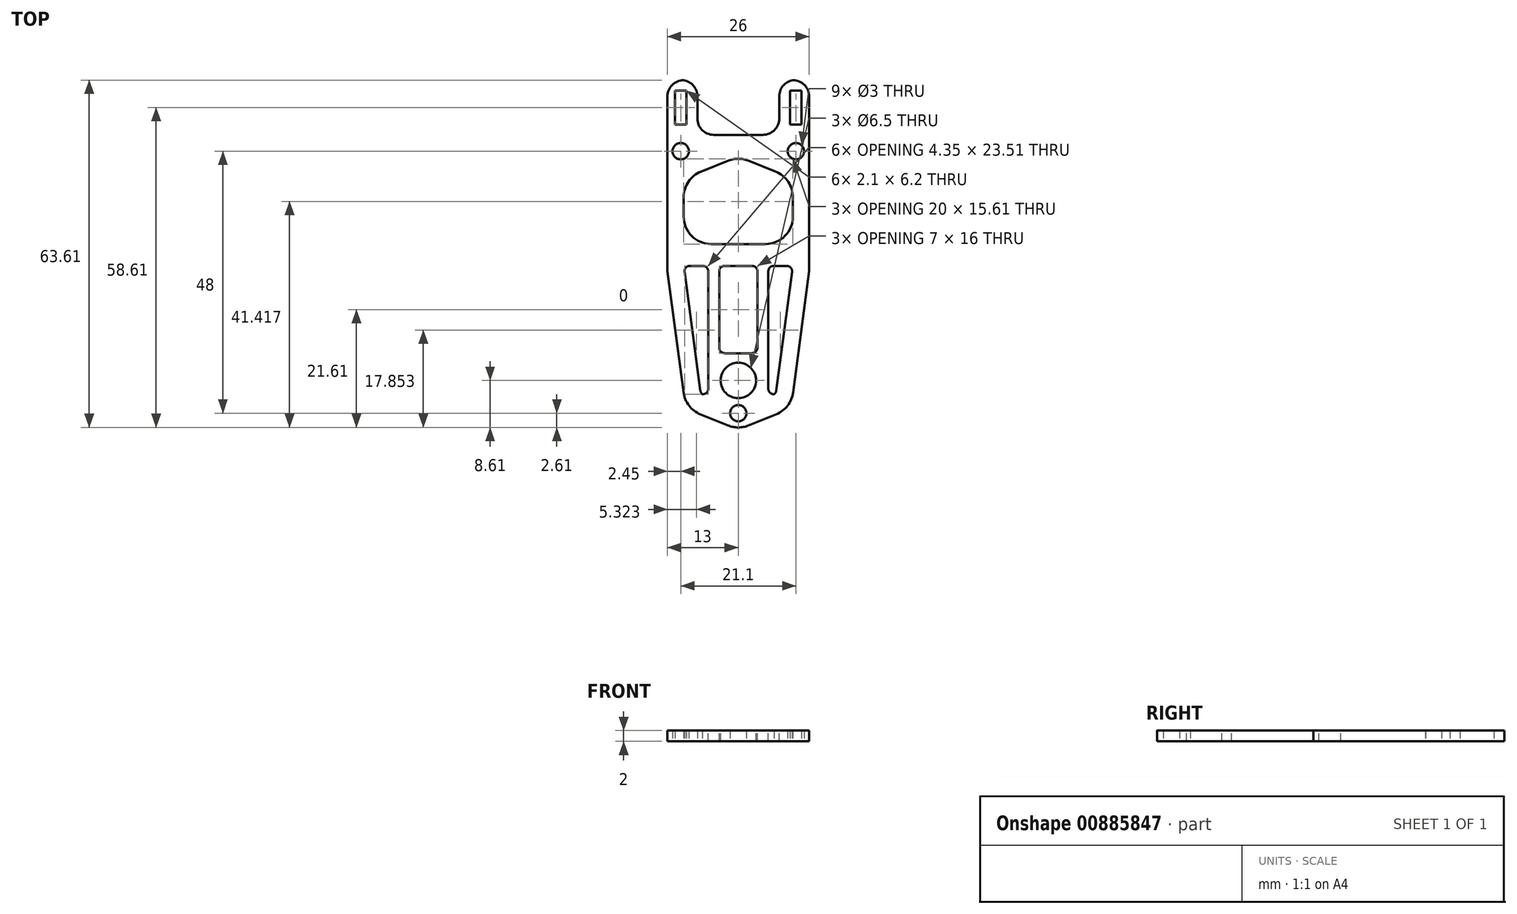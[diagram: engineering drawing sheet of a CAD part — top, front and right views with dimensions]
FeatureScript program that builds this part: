
annotation { "Feature Type Name" : "Feature", "Feature Type Description" : "" }
export const myFeature = defineFeature(function(context is Context, id is Id, definition is map)
    precondition{}
    {
        {
            var Q0;
            Q0=qCreatedBy(makeId("Top.planeOp"),FACE);
            var sketch = newSketch(context, id + "F0", { "sketchPlane" : qUnion([Q0])});
            skLineSegment(sketch, "E0.top", {"start": v(13, -32) * mm, "end": v(-13, -32) * mm});
            skLineSegment(sketch, "E0.left", {"start": v(13, 32) * mm, "end": v(13, -32) * mm});
            skLineSegment(sketch, "E0.right", {"start": v(-13, 32) * mm, "end": v(-13, -32) * mm});
            skPoint(sketch, "E0.middle", {"position": v(0, 0) * mm});
            skLineSegment(sketch, "E1.bottom", {"start": v(-11.6, 30.1) * mm, "end": v(-9.5, 30.1) * mm});
            skLineSegment(sketch, "E1.top", {"start": v(-11.6, 23.9) * mm, "end": v(-9.5, 23.9) * mm});
            skLineSegment(sketch, "E1.left", {"start": v(-11.6, 30.1) * mm, "end": v(-11.6, 23.9) * mm});
            skLineSegment(sketch, "E1.right", {"start": v(-9.5, 30.1) * mm, "end": v(-9.5, 23.9) * mm});
            skLineSegment(sketch, "E2.bottom", {"start": v(9.5, 30.1) * mm, "end": v(11.6, 30.1) * mm});
            skLineSegment(sketch, "E2.top", {"start": v(9.5, 23.9) * mm, "end": v(11.6, 23.9) * mm});
            skLineSegment(sketch, "E2.left", {"start": v(9.5, 30.1) * mm, "end": v(9.5, 23.9) * mm});
            skLineSegment(sketch, "E2.right", {"start": v(11.6, 30.1) * mm, "end": v(11.6, 23.9) * mm});
            skCircle(sketch, "E3", {"center": v(-10.55, 19) * mm, "radius": 1.5 * mm});
            skPoint(sketch, "E3.centerSnap0", {"position": v(-10.55, 30.1) * mm});
            skCircle(sketch, "E4", {"center": v(10.55, 19) * mm, "radius": 1.5 * mm});
            skPoint(sketch, "E4.centerSnap0", {"position": v(10.55, 30.1) * mm});
            skCircle(sketch, "E5", {"center": v(0, -29) * mm, "radius": 1.5 * mm});
            skLineSegment(sketch, "E6", {"start": v(-7.5, 32) * mm, "end": v(-7.5, 22) * mm});
            skLineSegment(sketch, "E7", {"start": v(-7.5, 22) * mm, "end": v(7.5, 22) * mm});
            skLineSegment(sketch, "E8", {"start": v(7.5, 22) * mm, "end": v(7.5, 32) * mm});
            skLineSegment(sketch, "E9", {"start": v(-13, 32) * mm, "end": v(-7.5, 32) * mm});
            skLineSegment(sketch, "E10", {"start": v(7.5, 32) * mm, "end": v(13, 32) * mm});
            skSolve(sketch);
        }
        {
            var Q0;
            Q0 = qSketchRegion(id + "F0", true);
            extrude(context, id + "F1", {"entities" : qUnion([Q0]), "depth" : 2 * mm, "offsetDistance" : 25 * mm});
        }
        {
            var Q0;
            Q0=makeQuery(id+"F1.opExtrude","SWEPT_EDGE",EDGE,{"disambiguationData":[OSD([sQuery(id+"F0.wireOp",EDGE,"E0.bottom"),sQuery(id+"F0.wireOp",EDGE,"E0.right")])]});
            var Q1;
            Q1=makeQuery(id+"F1.opExtrude","SWEPT_EDGE",EDGE,{"disambiguationData":[OSD([sQuery(id+"F0.wireOp",EDGE,"E0.bottom"),sQuery(id+"F0.wireOp",EDGE,"E0.left")])]});
            fillet(context, id + "F2", {"entities" : qUnion([Q0, Q1]), "radius" : 3 * mm, "tangentPropagation" : true, "allowEdgeOverflow" : false});
        }
        {
            var Q0;
            Q0=makeQuery(id+"F1.opExtrude","CAP_FACE",FACE,{"disambiguationData":[OSD([sQuery(id+"F0.wireOp",EDGE,"E0.bottom"),sQuery(id+"F0.wireOp",EDGE,"E0.top"),sQuery(id+"F0.wireOp",EDGE,"E0.left"),sQuery(id+"F0.wireOp",EDGE,"E0.right"),sQuery(id+"F0.wireOp",EDGE,"E1.bottom"),sQuery(id+"F0.wireOp",EDGE,"E1.top"),sQuery(id+"F0.wireOp",EDGE,"E1.left"),sQuery(id+"F0.wireOp",EDGE,"E1.right"),sQuery(id+"F0.wireOp",EDGE,"E2.bottom"),sQuery(id+"F0.wireOp",EDGE,"E2.top"),sQuery(id+"F0.wireOp",EDGE,"E2.left"),sQuery(id+"F0.wireOp",EDGE,"E2.right"),sQuery(id+"F0.wireOp",EDGE,"E3"),sQuery(id+"F0.wireOp",EDGE,"E4"),sQuery(id+"F0.wireOp",EDGE,"E5")])],"isStart":false});
            var sketch = newSketch(context, id + "F3", { "sketchPlane" : qUnion([Q0])});
            skLineSegment(sketch, "E11", {"start": v(-13, -3) * mm, "end": v(-13, -33) * mm});
            skLineSegment(sketch, "E12", {"start": v(-13, -33) * mm, "end": v(13, -33) * mm});
            skLineSegment(sketch, "E13", {"start": v(13, -33) * mm, "end": v(13, -3) * mm});
            skLineSegment(sketch, "E14", {"start": v(-13, -3) * mm, "end": v(-9.65, -28.1) * mm});
            skLineSegment(sketch, "E15", {"start": v(-9.65, -28.1) * mm, "end": v(0, -32) * mm});
            skLineSegment(sketch, "E16", {"start": v(0, -32) * mm, "end": v(9.65, -28.1) * mm});
            skLineSegment(sketch, "E17", {"start": v(9.65, -28.1) * mm, "end": v(13, -3) * mm});
            skSolve(sketch);
        }
        {
            var Q0;
            Q0 = qSketchRegion(id + "F3", true);
            extrude(context, id + "F4", {"entities" : qUnion([Q0]), "operationType" : NewBodyOperationType.REMOVE, "endBound" : BoundingType.THROUGH_ALL, "oppositeDirection" : true, "depth" : 25 * mm, "offsetDistance" : 25 * mm});
        }
        {
            var Q0;
            Q0=makeQuery(id+"F4.boolean.opBoolean","COPY",EDGE,{"derivedFrom":makeQuery(id+"F4.opExtrude","SWEPT_EDGE",EDGE,{"disambiguationData":[OSD([sQuery(id+"F0.wireOp",EDGE,"E0.right"),sQuery(id+"F3.wireOp",EDGE,"E11"),sQuery(id+"F3.wireOp",EDGE,"EHLrEQP2-Iu80-CbVW-FYZX-plo8Pidjctga")])]})});
            var Q1;
            Q1=makeQuery(id+"F4.boolean.opBoolean","COPY",EDGE,{"derivedFrom":makeQuery(id+"F4.opExtrude","SWEPT_EDGE",EDGE,{"disambiguationData":[OSD([sQuery(id+"F0.wireOp",EDGE,"E0.top"),sQuery(id+"F3.wireOp",EDGE,"fTFdpRz3-83xl-RkEX-MJaZ-tjTBTEaHAxbP"),sQuery(id+"F3.wireOp",EDGE,"EHLrEQP2-Iu80-CbVW-FYZX-plo8Pidjctga")])]})});
            var Q2;
            Q2=makeQuery(id+"F4.boolean.opBoolean","COPY",EDGE,{"derivedFrom":makeQuery(id+"F4.opExtrude","SWEPT_EDGE",EDGE,{"disambiguationData":[OSD([sQuery(id+"F0.wireOp",EDGE,"E0.left"),sQuery(id+"F3.wireOp",EDGE,"E13"),sQuery(id+"F3.wireOp",EDGE,"fTFdpRz3-83xl-RkEX-MJaZ-tjTBTEaHAxbP")])]})});
            var Q3;
            Q3=makeQuery(id+"F4.boolean.opBoolean","COPY",EDGE,{"derivedFrom":makeQuery(id+"F4.opExtrude","SWEPT_EDGE",EDGE,{"disambiguationData":[OSD([sQuery(id+"F3.wireOp",EDGE,"E16"),sQuery(id+"F3.wireOp",EDGE,"E17")])]})});
            var Q4;
            Q4=makeQuery(id+"F4.boolean.opBoolean","COPY",EDGE,{"derivedFrom":makeQuery(id+"F4.opExtrude","SWEPT_EDGE",EDGE,{"disambiguationData":[OSD([sQuery(id+"F3.wireOp",EDGE,"E14"),sQuery(id+"F3.wireOp",EDGE,"E15")])]})});
            fillet(context, id + "F5", {"entities" : qUnion([Q0, Q1, Q2, Q3, Q4]), "radius" : 5 * mm, "tangentPropagation" : true, "allowEdgeOverflow" : false});
        }
        {
            var Q0;
            Q0=makeQuery(id+"F1.opExtrude","SWEPT_EDGE",EDGE,{"disambiguationData":[OSD([sQuery(id+"F0.wireOp",EDGE,"E6"),sQuery(id+"F0.wireOp",EDGE,"E9")])]});
            var Q1;
            Q1=makeQuery(id+"F1.opExtrude","SWEPT_EDGE",EDGE,{"disambiguationData":[OSD([sQuery(id+"F0.wireOp",EDGE,"E6"),sQuery(id+"F0.wireOp",EDGE,"E7")])]});
            var Q2;
            Q2=makeQuery(id+"F1.opExtrude","SWEPT_EDGE",EDGE,{"disambiguationData":[OSD([sQuery(id+"F0.wireOp",EDGE,"E7"),sQuery(id+"F0.wireOp",EDGE,"E8")])]});
            var Q3;
            Q3=makeQuery(id+"F1.opExtrude","SWEPT_EDGE",EDGE,{"disambiguationData":[OSD([sQuery(id+"F0.wireOp",EDGE,"E8"),sQuery(id+"F0.wireOp",EDGE,"E10")])]});
            fillet(context, id + "F6", {"entities" : qUnion([Q0, Q1, Q2, Q3]), "radius" : 3 * mm, "tangentPropagation" : true, "allowEdgeOverflow" : false});
        }
        {
            var Q0;
            Q0=makeQuery(id+"F1.opExtrude","CAP_FACE",FACE,{"disambiguationData":[OSD([sQuery(id+"F0.wireOp",EDGE,"E0.top"),sQuery(id+"F0.wireOp",EDGE,"E0.left"),sQuery(id+"F0.wireOp",EDGE,"E0.right"),sQuery(id+"F0.wireOp",EDGE,"E1.bottom"),sQuery(id+"F0.wireOp",EDGE,"E1.top"),sQuery(id+"F0.wireOp",EDGE,"E1.left"),sQuery(id+"F0.wireOp",EDGE,"E1.right"),sQuery(id+"F0.wireOp",EDGE,"E2.bottom"),sQuery(id+"F0.wireOp",EDGE,"E2.top"),sQuery(id+"F0.wireOp",EDGE,"E2.left"),sQuery(id+"F0.wireOp",EDGE,"E2.right"),sQuery(id+"F0.wireOp",EDGE,"E3"),sQuery(id+"F0.wireOp",EDGE,"E4"),sQuery(id+"F0.wireOp",EDGE,"E5"),sQuery(id+"F0.wireOp",EDGE,"E6"),sQuery(id+"F0.wireOp",EDGE,"E7"),sQuery(id+"F0.wireOp",EDGE,"E8"),sQuery(id+"F0.wireOp",EDGE,"E9"),sQuery(id+"F0.wireOp",EDGE,"E10")])],"isStart":false});
            var sketch = newSketch(context, id + "F7", { "sketchPlane" : qUnion([Q0])});
            skLineSegment(sketch, "E18", {"start": v(0, 18) * mm, "end": v(-10, 14) * mm});
            skLineSegment(sketch, "E19", {"start": v(-10, 14) * mm, "end": v(-10, 2) * mm});
            skLineSegment(sketch, "E20", {"start": v(-10, 2) * mm, "end": v(10, 2) * mm});
            skLineSegment(sketch, "E21", {"start": v(10, 2) * mm, "end": v(10, 14) * mm});
            skLineSegment(sketch, "E22", {"start": v(10, 14) * mm, "end": v(0, 18) * mm});
            skLineSegment(sketch, "E23", {"start": v(-10, -2) * mm, "end": v(-6.87, -25.45) * mm});
            skLineSegment(sketch, "E24", {"start": v(-6.87, -25.45) * mm, "end": v(-5.5, -26) * mm});
            skLineSegment(sketch, "E25", {"start": v(-5.5, -26) * mm, "end": v(-5.5, -2) * mm});
            skLineSegment(sketch, "E26", {"start": v(-5.5, -2) * mm, "end": v(-10, -2) * mm});
            skLineSegment(sketch, "E27", {"start": v(10, -2) * mm, "end": v(6.87, -25.45) * mm});
            skLineSegment(sketch, "E28", {"start": v(6.87, -25.45) * mm, "end": v(5.5, -26) * mm});
            skLineSegment(sketch, "E29", {"start": v(5.5, -26) * mm, "end": v(5.5, -2) * mm});
            skLineSegment(sketch, "E30", {"start": v(5.5, -2) * mm, "end": v(10, -2) * mm});
            skLineSegment(sketch, "E31", {"start": v(-3.5, -18) * mm, "end": v(-3.5, -2) * mm});
            skLineSegment(sketch, "E32", {"start": v(-3.5, -2) * mm, "end": v(3.5, -2) * mm});
            skLineSegment(sketch, "E33", {"start": v(3.5, -2) * mm, "end": v(3.5, -18) * mm});
            skCircle(sketch, "E34", {"center": v(0, -23) * mm, "radius": 3.25 * mm});
            skLineSegment(sketch, "E35", {"start": v(-3.5, -18) * mm, "end": v(3.5, -18) * mm});
            skSolve(sketch);
        }
        {
            var Q0;
            Q0 = qSketchRegion(id + "F7", true);
            extrude(context, id + "F8", {"entities" : qUnion([Q0]), "operationType" : NewBodyOperationType.REMOVE, "endBound" : BoundingType.THROUGH_ALL, "oppositeDirection" : true, "depth" : 25 * mm, "offsetDistance" : 25 * mm});
        }
        {
            var Q0;
            Q0=makeQuery(id+"F8.boolean.opBoolean","COPY",EDGE,{"derivedFrom":makeQuery(id+"F8.opExtrude","SWEPT_EDGE",EDGE,{"disambiguationData":[OSD([sQuery(id+"F7.wireOp",EDGE,"E18"),sQuery(id+"F7.wireOp",EDGE,"E19")])]})});
            var Q1;
            Q1=makeQuery(id+"F8.boolean.opBoolean","COPY",EDGE,{"derivedFrom":makeQuery(id+"F8.opExtrude","SWEPT_EDGE",EDGE,{"disambiguationData":[OSD([sQuery(id+"F7.wireOp",EDGE,"E18"),sQuery(id+"F7.wireOp",EDGE,"E22")])]})});
            var Q2;
            Q2=makeQuery(id+"F8.boolean.opBoolean","COPY",EDGE,{"derivedFrom":makeQuery(id+"F8.opExtrude","SWEPT_EDGE",EDGE,{"disambiguationData":[OSD([sQuery(id+"F7.wireOp",EDGE,"E21"),sQuery(id+"F7.wireOp",EDGE,"E22")])]})});
            var Q3;
            Q3=makeQuery(id+"F8.boolean.opBoolean","COPY",EDGE,{"derivedFrom":makeQuery(id+"F8.opExtrude","SWEPT_EDGE",EDGE,{"disambiguationData":[OSD([sQuery(id+"F7.wireOp",EDGE,"E19"),sQuery(id+"F7.wireOp",EDGE,"E20")])]})});
            var Q4;
            Q4=makeQuery(id+"F8.boolean.opBoolean","COPY",EDGE,{"derivedFrom":makeQuery(id+"F8.opExtrude","SWEPT_EDGE",EDGE,{"disambiguationData":[OSD([sQuery(id+"F7.wireOp",EDGE,"E20"),sQuery(id+"F7.wireOp",EDGE,"E21")])]})});
            fillet(context, id + "F9", {"entities" : qUnion([Q0, Q1, Q2, Q3, Q4]), "radius" : 5 * mm, "tangentPropagation" : true, "allowEdgeOverflow" : false});
        }
        {
            var Q0;
            Q0=makeQuery(id+"F8.boolean.opBoolean","COPY",EDGE,{"derivedFrom":makeQuery(id+"F8.opExtrude","SWEPT_EDGE",EDGE,{"disambiguationData":[OSD([sQuery(id+"F7.wireOp",EDGE,"E23"),sQuery(id+"F7.wireOp",EDGE,"E26")])]})});
            var Q1;
            Q1=makeQuery(id+"F8.boolean.opBoolean","COPY",EDGE,{"derivedFrom":makeQuery(id+"F8.opExtrude","SWEPT_EDGE",EDGE,{"disambiguationData":[OSD([sQuery(id+"F7.wireOp",EDGE,"E31"),sQuery(id+"F7.wireOp",EDGE,"E32")])]})});
            var Q2;
            Q2=makeQuery(id+"F8.boolean.opBoolean","COPY",EDGE,{"derivedFrom":makeQuery(id+"F8.opExtrude","SWEPT_EDGE",EDGE,{"disambiguationData":[OSD([sQuery(id+"F7.wireOp",EDGE,"E29"),sQuery(id+"F7.wireOp",EDGE,"E30")])]})});
            var Q3;
            Q3=makeQuery(id+"F8.boolean.opBoolean","COPY",EDGE,{"derivedFrom":makeQuery(id+"F8.opExtrude","SWEPT_EDGE",EDGE,{"disambiguationData":[OSD([sQuery(id+"F7.wireOp",EDGE,"E25"),sQuery(id+"F7.wireOp",EDGE,"E26")])]})});
            var Q4;
            Q4=makeQuery(id+"F8.boolean.opBoolean","COPY",EDGE,{"derivedFrom":makeQuery(id+"F8.opExtrude","SWEPT_EDGE",EDGE,{"disambiguationData":[OSD([sQuery(id+"F7.wireOp",EDGE,"E32"),sQuery(id+"F7.wireOp",EDGE,"E33")])]})});
            var Q5;
            Q5=makeQuery(id+"F8.boolean.opBoolean","COPY",EDGE,{"derivedFrom":makeQuery(id+"F8.opExtrude","SWEPT_EDGE",EDGE,{"disambiguationData":[OSD([sQuery(id+"F7.wireOp",EDGE,"E27"),sQuery(id+"F7.wireOp",EDGE,"E30")])]})});
            var Q6;
            Q6=makeQuery(id+"F8.boolean.opBoolean","COPY",EDGE,{"derivedFrom":makeQuery(id+"F8.opExtrude","SWEPT_EDGE",EDGE,{"disambiguationData":[OSD([sQuery(id+"F7.wireOp",EDGE,"E31"),sQuery(id+"F7.wireOp",EDGE,"E35")])]})});
            var Q7;
            Q7=makeQuery(id+"F8.boolean.opBoolean","COPY",EDGE,{"derivedFrom":makeQuery(id+"F8.opExtrude","SWEPT_EDGE",EDGE,{"disambiguationData":[OSD([sQuery(id+"F7.wireOp",EDGE,"E33"),sQuery(id+"F7.wireOp",EDGE,"E35")])]})});
            var Q8;
            Q8=makeQuery(id+"F8.boolean.opBoolean","COPY",EDGE,{"derivedFrom":makeQuery(id+"F8.opExtrude","SWEPT_EDGE",EDGE,{"disambiguationData":[OSD([sQuery(id+"F7.wireOp",EDGE,"E23"),sQuery(id+"F7.wireOp",EDGE,"E24")])]})});
            var Q9;
            Q9=makeQuery(id+"F8.boolean.opBoolean","COPY",EDGE,{"derivedFrom":makeQuery(id+"F8.opExtrude","SWEPT_EDGE",EDGE,{"disambiguationData":[OSD([sQuery(id+"F7.wireOp",EDGE,"E27"),sQuery(id+"F7.wireOp",EDGE,"E28")])]})});
            var Q10;
            Q10=makeQuery(id+"F8.boolean.opBoolean","COPY",EDGE,{"derivedFrom":makeQuery(id+"F8.opExtrude","SWEPT_EDGE",EDGE,{"disambiguationData":[OSD([sQuery(id+"F7.wireOp",EDGE,"E28"),sQuery(id+"F7.wireOp",EDGE,"E29")])]})});
            var Q11;
            Q11=makeQuery(id+"F8.boolean.opBoolean","COPY",EDGE,{"derivedFrom":makeQuery(id+"F8.opExtrude","SWEPT_EDGE",EDGE,{"disambiguationData":[OSD([sQuery(id+"F7.wireOp",EDGE,"E24"),sQuery(id+"F7.wireOp",EDGE,"E25")])]})});
            fillet(context, id + "F10", {"entities" : qUnion([Q0, Q1, Q2, Q3, Q4, Q5, Q6, Q7, Q8, Q9, Q10, Q11]), "radius" : 1 * mm, "tangentPropagation" : true, "allowEdgeOverflow" : false});
        }
    });
